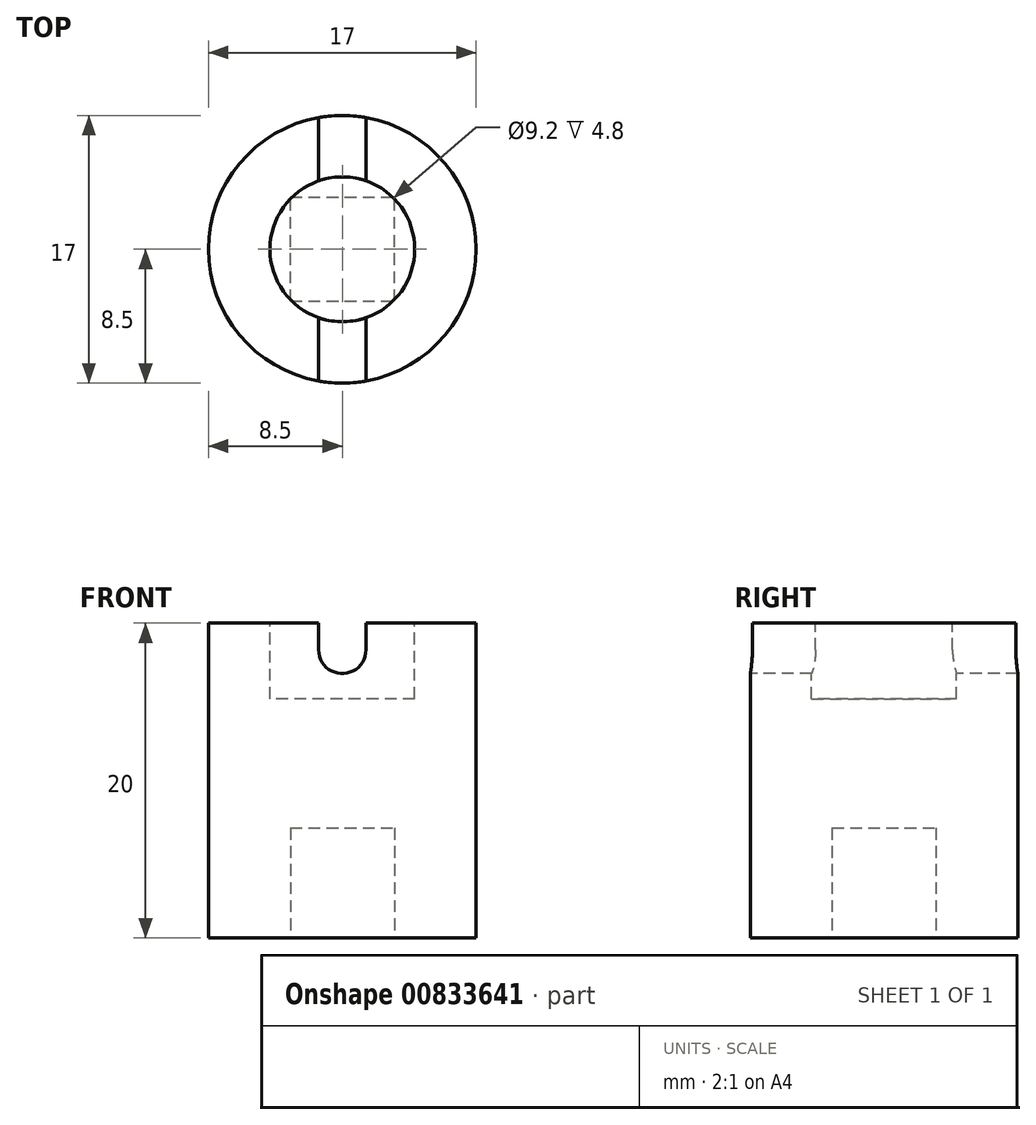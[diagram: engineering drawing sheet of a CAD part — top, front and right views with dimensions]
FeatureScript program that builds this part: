
annotation { "Feature Type Name" : "Feature", "Feature Type Description" : "" }
export const myFeature = defineFeature(function(context is Context, id is Id, definition is map)
    precondition{}
    {
        {
            var Q0;
            Q0=qCreatedBy(makeId("Top.planeOp"),FACE);
            var sketch = newSketch(context, id + "F0", { "sketchPlane" : qUnion([Q0])});
            skCircle(sketch, "E0", {"center": v(0, 0) * mm, "radius": 8.5 * mm});
            skSolve(sketch);
        }
        {
            var Q0;
            Q0 = qSketchRegion(id + "F0", true);
            extrude(context, id + "F1", {"entities" : qUnion([Q0]), "depth" : 20 * mm, "offsetDistance" : 25 * mm});
        }
        {
            var Q0;
            Q0=makeQuery(id+"F1.opExtrude","CAP_FACE",FACE,{"disambiguationData":[OSD([sQuery(id+"F0.wireOp",EDGE,"E0")])],"isStart":false});
            var sketch = newSketch(context, id + "F2", { "sketchPlane" : qUnion([Q0])});
            skCircle(sketch, "E1", {"center": v(0, 0) * mm, "radius": 4.6 * mm});
            skSolve(sketch);
        }
        {
            var Q0;
            Q0 = qSketchRegion(id + "F2", true);
            extrude(context, id + "F3", {"entities" : qUnion([Q0]), "operationType" : NewBodyOperationType.REMOVE, "oppositeDirection" : true, "depth" : 4.8 * mm, "offsetDistance" : 25 * mm});
        }
        {
            var Q0;
            Q0=qCreatedBy(makeId("Front.planeOp"),FACE);
            var sketch = newSketch(context, id + "F4", { "sketchPlane" : qUnion([Q0])});
            skArc(sketch, "E2", {"start": v(-1.5, 18.3) * mm, "mid": v(0, 16.8) * mm, "end": v(1.5, 18.3) * mm});
            skLineSegment(sketch, "E3", {"start": v(1.5, 18.3) * mm, "end": v(1.5, 20) * mm});
            skLineSegment(sketch, "E4", {"start": v(1.5, 20) * mm, "end": v(-1.5, 20) * mm});
            skLineSegment(sketch, "E5", {"start": v(-1.5, 20) * mm, "end": v(-1.5, 18.3) * mm});
            skSolve(sketch);
        }
        {
            var Q0;
            Q0 = qSketchRegion(id + "F4", true);
            extrude(context, id + "F5", {"entities" : qUnion([Q0]), "operationType" : NewBodyOperationType.REMOVE, "endBound" : BoundingType.SYMMETRIC, "oppositeDirection" : true, "depth" : 25 * mm, "offsetDistance" : 25 * mm});
        }
        {
            var Q0;
            Q0=makeQuery(id+"F1.opExtrude","CAP_FACE",FACE,{"disambiguationData":[OSD([sQuery(id+"F0.wireOp",EDGE,"E0")])],"isStart":true});
            var sketch = newSketch(context, id + "F6", { "sketchPlane" : qUnion([Q0])});
            skLineSegment(sketch, "E6.bottom", {"start": v(-3.3, 3.3) * mm, "end": v(3.3, 3.3) * mm});
            skLineSegment(sketch, "E6.top", {"start": v(-3.3, -3.3) * mm, "end": v(3.3, -3.3) * mm});
            skLineSegment(sketch, "E6.left", {"start": v(-3.3, 3.3) * mm, "end": v(-3.3, -3.3) * mm});
            skLineSegment(sketch, "E6.right", {"start": v(3.3, 3.3) * mm, "end": v(3.3, -3.3) * mm});
            skSolve(sketch);
        }
        {
            var Q0;
            Q0 = qSketchRegion(id + "F6", true);
            extrude(context, id + "F7", {"entities" : qUnion([Q0]), "operationType" : NewBodyOperationType.REMOVE, "oppositeDirection" : true, "depth" : 7 * mm, "offsetDistance" : 25 * mm});
        }
    });
